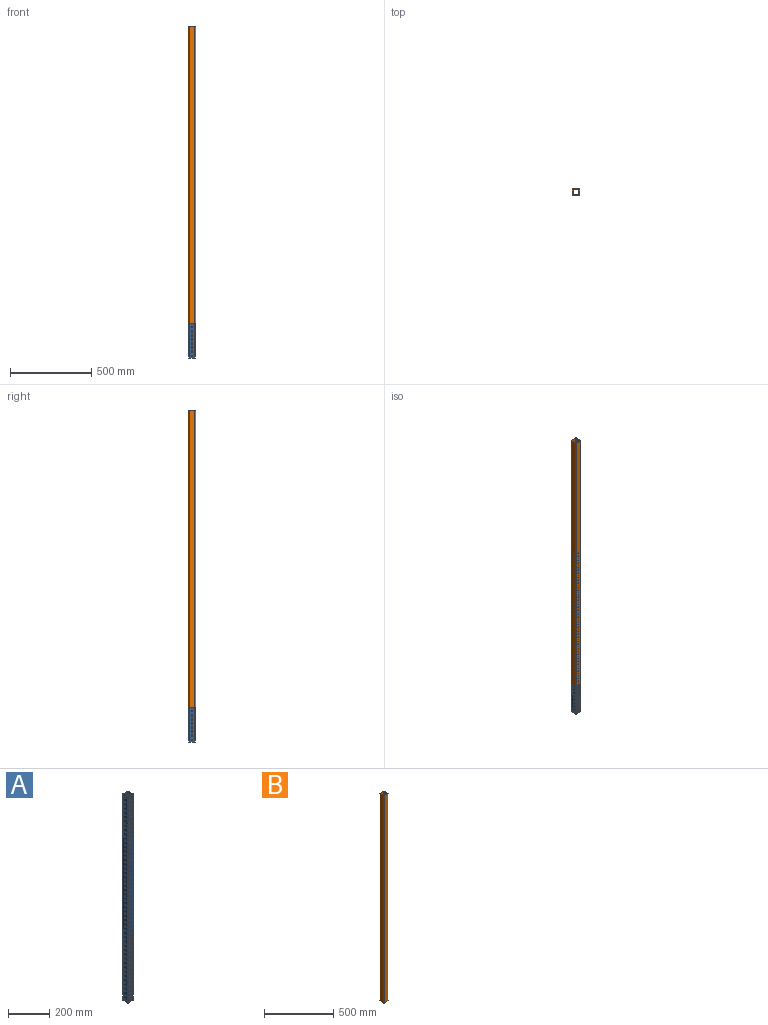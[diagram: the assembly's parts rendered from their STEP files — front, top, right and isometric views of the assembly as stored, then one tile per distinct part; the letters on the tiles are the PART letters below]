
ASSEMBLY  parts=2 mates=1
PART A: 210 faces, bbox 38.1x38.1x1219.2 mm
  f0: cylinder r=5.56mm len=11.11mm, axis (1,0,0), area 93.1mm2, adj f201,f203
  f1: cylinder r=5.56mm len=11.11mm, axis (1,0,0), area 93.1mm2, adj f197,f207
  f2: cylinder r=5.56mm len=11.11mm, axis (1,0,0), area 93.1mm2, adj f201,f203
  f3: cylinder r=5.56mm len=11.11mm, axis (1,0,0), area 93.1mm2, adj f197,f207
  f4: cylinder r=5.56mm len=11.11mm, axis (1,0,0), area 93.1mm2, adj f201,f203
  f5: cylinder r=5.56mm len=11.11mm, axis (1,0,0), area 93.1mm2, adj f197,f207
  f6: cylinder r=5.56mm len=11.11mm, axis (1,0,0), area 93.1mm2, adj f201,f203
  f7: cylinder r=5.56mm len=11.11mm, axis (1,0,0), area 93.1mm2, adj f197,f207
  f8: cylinder r=5.56mm len=11.11mm, axis (1,0,0), area 93.1mm2, adj f201,f203
  f9: cylinder r=5.56mm len=11.11mm, axis (1,0,0), area 93.1mm2, adj f197,f207
  f10: cylinder r=5.56mm len=11.11mm, axis (1,0,0), area 93.1mm2, adj f201,f203
  f11: cylinder r=5.56mm len=11.11mm, axis (1,0,0), area 93.1mm2, adj f197,f207
  f12: cylinder r=5.56mm len=11.11mm, axis (1,0,0), area 93.1mm2, adj f201,f203
  f13: cylinder r=5.56mm len=11.11mm, axis (1,0,0), area 93.1mm2, adj f197,f207
  f14: cylinder r=5.56mm len=11.11mm, axis (1,0,0), area 93.1mm2, adj f201,f203
  f15: cylinder r=5.56mm len=11.11mm, axis (1,0,0), area 93.1mm2, adj f197,f207
  f16: cylinder r=5.56mm len=11.11mm, axis (1,0,0), area 93.1mm2, adj f201,f203
  f17: cylinder r=5.56mm len=11.11mm, axis (1,0,0), area 93.1mm2, adj f197,f207
  f18: cylinder r=5.56mm len=11.11mm, axis (1,0,0), area 93.1mm2, adj f201,f203
  f19: cylinder r=5.56mm len=11.11mm, axis (1,0,0), area 93.1mm2, adj f197,f207
  f20: cylinder r=5.56mm len=11.11mm, axis (1,0,0), area 93.1mm2, adj f201,f203
  f21: cylinder r=5.56mm len=11.11mm, axis (1,0,0), area 93.1mm2, adj f197,f207
  f22: cylinder r=5.56mm len=11.11mm, axis (1,0,0), area 93.1mm2, adj f201,f203
  f23: cylinder r=5.56mm len=11.11mm, axis (1,0,0), area 93.1mm2, adj f197,f207
  f24: cylinder r=5.56mm len=11.11mm, axis (1,0,0), area 93.1mm2, adj f201,f203
  f25: cylinder r=5.56mm len=11.11mm, axis (1,0,0), area 93.1mm2, adj f197,f207
  f26: cylinder r=5.56mm len=11.11mm, axis (1,0,0), area 93.1mm2, adj f201,f203
  f27: cylinder r=5.56mm len=11.11mm, axis (1,0,0), area 93.1mm2, adj f197,f207
  f28: cylinder r=5.56mm len=11.11mm, axis (1,0,0), area 93.1mm2, adj f201,f203
  f29: cylinder r=5.56mm len=11.11mm, axis (1,0,0), area 93.1mm2, adj f197,f207
  f30: cylinder r=5.56mm len=11.11mm, axis (1,0,0), area 93.1mm2, adj f201,f203
  f31: cylinder r=5.56mm len=11.11mm, axis (1,0,0), area 93.1mm2, adj f197,f207
  f32: cylinder r=5.56mm len=11.11mm, axis (1,0,0), area 93.1mm2, adj f201,f203
  f33: cylinder r=5.56mm len=11.11mm, axis (1,0,0), area 93.1mm2, adj f197,f207
  f34: cylinder r=5.56mm len=11.11mm, axis (1,0,0), area 93.1mm2, adj f201,f203
  f35: cylinder r=5.56mm len=11.11mm, axis (1,0,0), area 93.1mm2, adj f197,f207
  f36: cylinder r=5.56mm len=11.11mm, axis (1,0,0), area 93.1mm2, adj f201,f203
  f37: cylinder r=5.56mm len=11.11mm, axis (1,0,0), area 93.1mm2, adj f197,f207
  f38: cylinder r=5.56mm len=11.11mm, axis (1,0,0), area 93.1mm2, adj f201,f203
  f39: cylinder r=5.56mm len=11.11mm, axis (1,0,0), area 93.1mm2, adj f197,f207
  f40: cylinder r=5.56mm len=11.11mm, axis (1,0,0), area 93.1mm2, adj f201,f203
  f41: cylinder r=5.56mm len=11.11mm, axis (1,0,0), area 93.1mm2, adj f197,f207
  f42: cylinder r=5.56mm len=11.11mm, axis (1,0,0), area 93.1mm2, adj f201,f203
  f43: cylinder r=5.56mm len=11.11mm, axis (1,0,0), area 93.1mm2, adj f197,f207
  f44: cylinder r=5.56mm len=11.11mm, axis (1,0,0), area 93.1mm2, adj f201,f203
  f45: cylinder r=5.56mm len=11.11mm, axis (1,0,0), area 93.1mm2, adj f197,f207
  f46: cylinder r=5.56mm len=11.11mm, axis (1,0,0), area 93.1mm2, adj f201,f203
  f47: cylinder r=5.56mm len=11.11mm, axis (1,0,0), area 93.1mm2, adj f197,f207
  f48: cylinder r=5.56mm len=11.11mm, axis (1,0,0), area 93.1mm2, adj f201,f203
  f49: cylinder r=5.56mm len=11.11mm, axis (1,0,0), area 93.1mm2, adj f197,f207
  f50: cylinder r=5.56mm len=11.11mm, axis (1,0,0), area 93.1mm2, adj f201,f203
  f51: cylinder r=5.56mm len=11.11mm, axis (1,0,0), area 93.1mm2, adj f197,f207
  f52: cylinder r=5.56mm len=11.11mm, axis (1,0,0), area 93.1mm2, adj f201,f203
  f53: cylinder r=5.56mm len=11.11mm, axis (1,0,0), area 93.1mm2, adj f197,f207
  f54: cylinder r=5.56mm len=11.11mm, axis (1,0,0), area 93.1mm2, adj f201,f203
  f55: cylinder r=5.56mm len=11.11mm, axis (1,0,0), area 93.1mm2, adj f197,f207
  f56: cylinder r=5.56mm len=11.11mm, axis (1,0,0), area 93.1mm2, adj f201,f203
  f57: cylinder r=5.56mm len=11.11mm, axis (1,0,0), area 93.1mm2, adj f197,f207
  f58: cylinder r=5.56mm len=11.11mm, axis (1,0,0), area 93.1mm2, adj f201,f203
  f59: cylinder r=5.56mm len=11.11mm, axis (1,0,0), area 93.1mm2, adj f197,f207
  f60: cylinder r=5.56mm len=11.11mm, axis (1,0,0), area 93.1mm2, adj f201,f203
  f61: cylinder r=5.56mm len=11.11mm, axis (1,0,0), area 93.1mm2, adj f197,f207
  f62: cylinder r=5.56mm len=11.11mm, axis (1,0,0), area 93.1mm2, adj f201,f203
  f63: cylinder r=5.56mm len=11.11mm, axis (1,0,0), area 93.1mm2, adj f197,f207
  f64: cylinder r=5.56mm len=11.11mm, axis (1,0,0), area 93.1mm2, adj f201,f203
  f65: cylinder r=5.56mm len=11.11mm, axis (1,0,0), area 93.1mm2, adj f197,f207
  f66: cylinder r=5.56mm len=11.11mm, axis (1,0,0), area 93.1mm2, adj f201,f203
  f67: cylinder r=5.56mm len=11.11mm, axis (1,0,0), area 93.1mm2, adj f197,f207
  f68: cylinder r=5.56mm len=11.11mm, axis (1,0,0), area 93.1mm2, adj f201,f203
  f69: cylinder r=5.56mm len=11.11mm, axis (1,0,0), area 93.1mm2, adj f197,f207
  f70: cylinder r=5.56mm len=11.11mm, axis (1,0,0), area 93.1mm2, adj f201,f203
  f71: cylinder r=5.56mm len=11.11mm, axis (1,0,0), area 93.1mm2, adj f197,f207
  f72: cylinder r=5.56mm len=11.11mm, axis (1,0,0), area 93.1mm2, adj f201,f203
  f73: cylinder r=5.56mm len=11.11mm, axis (1,0,0), area 93.1mm2, adj f197,f207
  f74: cylinder r=5.56mm len=11.11mm, axis (1,0,0), area 93.1mm2, adj f201,f203
  f75: cylinder r=5.56mm len=11.11mm, axis (1,0,0), area 93.1mm2, adj f197,f207
  f76: cylinder r=5.56mm len=11.11mm, axis (1,0,0), area 93.1mm2, adj f201,f203
  f77: cylinder r=5.56mm len=11.11mm, axis (1,0,0), area 93.1mm2, adj f197,f207
  f78: cylinder r=5.56mm len=11.11mm, axis (1,0,0), area 93.1mm2, adj f201,f203
  f79: cylinder r=5.56mm len=11.11mm, axis (1,0,0), area 93.1mm2, adj f197,f207
  f80: cylinder r=5.56mm len=11.11mm, axis (1,0,0), area 93.1mm2, adj f201,f203
  f81: cylinder r=5.56mm len=11.11mm, axis (1,0,0), area 93.1mm2, adj f197,f207
  f82: cylinder r=5.56mm len=11.11mm, axis (1,0,0), area 93.1mm2, adj f201,f203
  f83: cylinder r=5.56mm len=11.11mm, axis (1,0,0), area 93.1mm2, adj f197,f207
  f84: cylinder r=5.56mm len=11.11mm, axis (1,0,0), area 93.1mm2, adj f201,f203
  f85: cylinder r=5.56mm len=11.11mm, axis (1,0,0), area 93.1mm2, adj f197,f207
  f86: cylinder r=5.56mm len=11.11mm, axis (1,0,0), area 93.1mm2, adj f201,f203
  f87: cylinder r=5.56mm len=11.11mm, axis (1,0,0), area 93.1mm2, adj f197,f207
  f88: cylinder r=5.56mm len=11.11mm, axis (1,0,0), area 93.1mm2, adj f201,f203
  f89: cylinder r=5.56mm len=11.11mm, axis (1,0,0), area 93.1mm2, adj f197,f207
  f90: cylinder r=5.56mm len=11.11mm, axis (1,0,0), area 93.1mm2, adj f201,f203
  f91: cylinder r=5.56mm len=11.11mm, axis (1,0,0), area 93.1mm2, adj f197,f207
  f92: cylinder r=5.56mm len=11.11mm, axis (1,0,0), area 93.1mm2, adj f201,f203
  f93: cylinder r=5.56mm len=11.11mm, axis (1,0,0), area 93.1mm2, adj f197,f207
  f94: cylinder r=5.56mm len=11.11mm, axis (1,0,0), area 93.1mm2, adj f201,f203
  f95: cylinder r=5.56mm len=11.11mm, axis (1,0,0), area 93.1mm2, adj f197,f207
  f96: cylinder r=5.56mm len=11.11mm, axis (0,1,0), area 93.1mm2, adj f199,f209
  f97: cylinder r=5.56mm len=11.11mm, axis (0,1,0), area 93.1mm2, adj f199,f209
  f98: cylinder r=5.56mm len=11.11mm, axis (0,1,0), area 93.1mm2, adj f199,f209
  f99: cylinder r=5.56mm len=11.11mm, axis (0,1,0), area 93.1mm2, adj f199,f209
  f100: cylinder r=5.56mm len=11.11mm, axis (0,1,0), area 93.1mm2, adj f199,f209
  f101: cylinder r=5.56mm len=11.11mm, axis (0,1,0), area 93.1mm2, adj f199,f209
  f102: cylinder r=5.56mm len=11.11mm, axis (0,1,0), area 93.1mm2, adj f199,f209
  f103: cylinder r=5.56mm len=11.11mm, axis (0,1,0), area 93.1mm2, adj f199,f209
  f104: cylinder r=5.56mm len=11.11mm, axis (0,1,0), area 93.1mm2, adj f199,f209
  f105: cylinder r=5.56mm len=11.11mm, axis (0,1,0), area 93.1mm2, adj f199,f209
  f106: cylinder r=5.56mm len=11.11mm, axis (0,1,0), area 93.1mm2, adj f199,f209
  f107: cylinder r=5.56mm len=11.11mm, axis (0,1,0), area 93.1mm2, adj f199,f209
  f108: cylinder r=5.56mm len=11.11mm, axis (0,1,0), area 93.1mm2, adj f199,f209
  f109: cylinder r=5.56mm len=11.11mm, axis (0,1,0), area 93.1mm2, adj f199,f209
  f110: cylinder r=5.56mm len=11.11mm, axis (0,1,0), area 93.1mm2, adj f199,f209
  f111: cylinder r=5.56mm len=11.11mm, axis (0,1,0), area 93.1mm2, adj f199,f209
  f112: cylinder r=5.56mm len=11.11mm, axis (0,1,0), area 93.1mm2, adj f199,f209
  f113: cylinder r=5.56mm len=11.11mm, axis (0,1,0), area 93.1mm2, adj f199,f209
  f114: cylinder r=5.56mm len=11.11mm, axis (0,1,0), area 93.1mm2, adj f199,f209
  f115: cylinder r=5.56mm len=11.11mm, axis (0,1,0), area 93.1mm2, adj f199,f209
  f116: cylinder r=5.56mm len=11.11mm, axis (0,1,0), area 93.1mm2, adj f199,f209
  f117: cylinder r=5.56mm len=11.11mm, axis (0,1,0), area 93.1mm2, adj f199,f209
  f118: cylinder r=5.56mm len=11.11mm, axis (0,1,0), area 93.1mm2, adj f199,f209
  f119: cylinder r=5.56mm len=11.11mm, axis (0,1,0), area 93.1mm2, adj f199,f209
  f120: cylinder r=5.56mm len=11.11mm, axis (0,1,0), area 93.1mm2, adj f199,f209
  f121: cylinder r=5.56mm len=11.11mm, axis (0,1,0), area 93.1mm2, adj f199,f209
  f122: cylinder r=5.56mm len=11.11mm, axis (0,1,0), area 93.1mm2, adj f199,f209
  f123: cylinder r=5.56mm len=11.11mm, axis (0,1,0), area 93.1mm2, adj f199,f209
  f124: cylinder r=5.56mm len=11.11mm, axis (0,1,0), area 93.1mm2, adj f199,f209
  f125: cylinder r=5.56mm len=11.11mm, axis (0,1,0), area 93.1mm2, adj f199,f209
  f126: cylinder r=5.56mm len=11.11mm, axis (0,1,0), area 93.1mm2, adj f199,f209
  f127: cylinder r=5.56mm len=11.11mm, axis (0,1,0), area 93.1mm2, adj f199,f209
  f128: cylinder r=5.56mm len=11.11mm, axis (0,1,0), area 93.1mm2, adj f199,f209
  f129: cylinder r=5.56mm len=11.11mm, axis (0,1,0), area 93.1mm2, adj f199,f209
  f130: cylinder r=5.56mm len=11.11mm, axis (0,1,0), area 93.1mm2, adj f199,f209
  f131: cylinder r=5.56mm len=11.11mm, axis (0,1,0), area 93.1mm2, adj f199,f209
  f132: cylinder r=5.56mm len=11.11mm, axis (0,1,0), area 93.1mm2, adj f199,f209
  f133: cylinder r=5.56mm len=11.11mm, axis (0,1,0), area 93.1mm2, adj f199,f209
  f134: cylinder r=5.56mm len=11.11mm, axis (0,1,0), area 93.1mm2, adj f199,f209
  f135: cylinder r=5.56mm len=11.11mm, axis (0,1,0), area 93.1mm2, adj f199,f209
  f136: cylinder r=5.56mm len=11.11mm, axis (0,1,0), area 93.1mm2, adj f199,f209
  f137: cylinder r=5.56mm len=11.11mm, axis (0,1,0), area 93.1mm2, adj f199,f209
  f138: cylinder r=5.56mm len=11.11mm, axis (0,1,0), area 93.1mm2, adj f199,f209
  f139: cylinder r=5.56mm len=11.11mm, axis (0,1,0), area 93.1mm2, adj f199,f209
  f140: cylinder r=5.56mm len=11.11mm, axis (0,1,0), area 93.1mm2, adj f199,f209
  f141: cylinder r=5.56mm len=11.11mm, axis (0,1,0), area 93.1mm2, adj f199,f209
  f142: cylinder r=5.56mm len=11.11mm, axis (0,1,0), area 93.1mm2, adj f199,f209
  f143: cylinder r=5.56mm len=11.11mm, axis (0,1,0), area 93.1mm2, adj f195,f205
  f144: cylinder r=5.56mm len=11.11mm, axis (0,1,0), area 93.1mm2, adj f195,f205
  f145: cylinder r=5.56mm len=11.11mm, axis (0,1,0), area 93.1mm2, adj f195,f205
  f146: cylinder r=5.56mm len=11.11mm, axis (0,1,0), area 93.1mm2, adj f195,f205
  f147: cylinder r=5.56mm len=11.11mm, axis (0,1,0), area 93.1mm2, adj f195,f205
  f148: cylinder r=5.56mm len=11.11mm, axis (0,1,0), area 93.1mm2, adj f195,f205
  f149: cylinder r=5.56mm len=11.11mm, axis (0,1,0), area 93.1mm2, adj f195,f205
  f150: cylinder r=5.56mm len=11.11mm, axis (0,1,0), area 93.1mm2, adj f195,f205
  f151: cylinder r=5.56mm len=11.11mm, axis (0,1,0), area 93.1mm2, adj f195,f205
  f152: cylinder r=5.56mm len=11.11mm, axis (0,1,0), area 93.1mm2, adj f195,f205
  f153: cylinder r=5.56mm len=11.11mm, axis (0,1,0), area 93.1mm2, adj f195,f205
  f154: cylinder r=5.56mm len=11.11mm, axis (0,1,0), area 93.1mm2, adj f195,f205
  f155: cylinder r=5.56mm len=11.11mm, axis (0,1,0), area 93.1mm2, adj f195,f205
  f156: cylinder r=5.56mm len=11.11mm, axis (0,1,0), area 93.1mm2, adj f195,f205
  f157: cylinder r=5.56mm len=11.11mm, axis (0,1,0), area 93.1mm2, adj f195,f205
  f158: cylinder r=5.56mm len=11.11mm, axis (0,1,0), area 93.1mm2, adj f195,f205
  f159: cylinder r=5.56mm len=11.11mm, axis (0,1,0), area 93.1mm2, adj f195,f205
  f160: cylinder r=5.56mm len=11.11mm, axis (0,1,0), area 93.1mm2, adj f195,f205
  f161: cylinder r=5.56mm len=11.11mm, axis (0,1,0), area 93.1mm2, adj f195,f205
  f162: cylinder r=5.56mm len=11.11mm, axis (0,1,0), area 93.1mm2, adj f195,f205
  f163: cylinder r=5.56mm len=11.11mm, axis (0,1,0), area 93.1mm2, adj f195,f205
  f164: cylinder r=5.56mm len=11.11mm, axis (0,1,0), area 93.1mm2, adj f195,f205
  f165: cylinder r=5.56mm len=11.11mm, axis (0,1,0), area 93.1mm2, adj f195,f205
  f166: cylinder r=5.56mm len=11.11mm, axis (0,1,0), area 93.1mm2, adj f195,f205
  f167: cylinder r=5.56mm len=11.11mm, axis (0,1,0), area 93.1mm2, adj f195,f205
  f168: cylinder r=5.56mm len=11.11mm, axis (0,1,0), area 93.1mm2, adj f195,f205
  f169: cylinder r=5.56mm len=11.11mm, axis (0,1,0), area 93.1mm2, adj f195,f205
  f170: cylinder r=5.56mm len=11.11mm, axis (0,1,0), area 93.1mm2, adj f195,f205
  f171: cylinder r=5.56mm len=11.11mm, axis (0,1,0), area 93.1mm2, adj f195,f205
  f172: cylinder r=5.56mm len=11.11mm, axis (0,1,0), area 93.1mm2, adj f195,f205
  f173: cylinder r=5.56mm len=11.11mm, axis (0,1,0), area 93.1mm2, adj f195,f205
  f174: cylinder r=5.56mm len=11.11mm, axis (0,1,0), area 93.1mm2, adj f195,f205
  f175: cylinder r=5.56mm len=11.11mm, axis (0,1,0), area 93.1mm2, adj f195,f205
  f176: cylinder r=5.56mm len=11.11mm, axis (0,1,0), area 93.1mm2, adj f195,f205
  f177: cylinder r=5.56mm len=11.11mm, axis (0,1,0), area 93.1mm2, adj f195,f205
  f178: cylinder r=5.56mm len=11.11mm, axis (0,1,0), area 93.1mm2, adj f195,f205
  f179: cylinder r=5.56mm len=11.11mm, axis (0,1,0), area 93.1mm2, adj f195,f205
  f180: cylinder r=5.56mm len=11.11mm, axis (0,1,0), area 93.1mm2, adj f195,f205
  f181: cylinder r=5.56mm len=11.11mm, axis (0,1,0), area 93.1mm2, adj f195,f205
  f182: cylinder r=5.56mm len=11.11mm, axis (0,1,0), area 93.1mm2, adj f195,f205
  f183: cylinder r=5.56mm len=11.11mm, axis (0,1,0), area 93.1mm2, adj f195,f205
  f184: cylinder r=5.56mm len=11.11mm, axis (0,1,0), area 93.1mm2, adj f195,f205
  f185: cylinder r=5.56mm len=11.11mm, axis (0,1,0), area 93.1mm2, adj f195,f205
  f186: cylinder r=5.56mm len=11.11mm, axis (0,1,0), area 93.1mm2, adj f195,f205
  f187: cylinder r=5.56mm len=11.11mm, axis (0,1,0), area 93.1mm2, adj f195,f205
  f188: cylinder r=5.56mm len=11.11mm, axis (0,1,0), area 93.1mm2, adj f195,f205
  f189: cylinder r=5.56mm len=11.11mm, axis (0,1,0), area 93.1mm2, adj f195,f205
  f190: cylinder r=5.56mm len=11.11mm, axis (0,1,0), area 93.1mm2, adj f195,f205
  f191: cylinder r=5.56mm len=11.11mm, axis (0,1,0), area 93.1mm2, adj f199,f209
  f192: plane 38.1x38.1mm, normal (0,0,1), area 364.9mm2, adj f194,f195,f196,f197,f198,f199,f200,f201
  f193: plane 38.1x38.1mm, normal (0,0,-1), area 364.9mm2, adj f194,f195,f196,f197,f198,f199,f200,f201
  f194: cylinder r=4.19mm len=1219.2mm, axis (0,0,-1), area 8026.2mm2, adj f192,f193,f195,f201
  f195: plane 1219.2x29.72mm, normal (0,-1,0), area 31576.8mm2, adj f143,f144,f145,f146,f147,f148,f149,f150
  f196: cylinder r=4.19mm len=1219.2mm, axis (0,0,-1), area 8026.2mm2, adj f192,f193,f195,f197
  f197: plane 1219.2x29.72mm, normal (1,0,0), area 31576.8mm2, adj f1,f3,f5,f7,f9,f11,f13,f15
  f198: cylinder r=4.19mm len=1219.2mm, axis (0,0,-1), area 8026.2mm2, adj f192,f193,f197,f199
  f199: plane 1219.2x29.72mm, normal (0,1,0), area 31576.8mm2, adj f96,f97,f98,f99,f100,f101,f102,f103
  f200: cylinder r=4.19mm len=1219.2mm, axis (0,0,-1), area 8026.2mm2, adj f192,f193,f199,f201
  f201: plane 1219.2x29.72mm, normal (-1,0,0), area 31576.8mm2, adj f0,f2,f4,f6,f8,f10,f12,f14
  f202: cylinder r=1.52mm len=1219.2mm, axis (0,0,-1), area 2918.6mm2, adj f192,f193,f203,f209
  f203: plane 1219.2x29.72mm, normal (1,0,0), area 31576.8mm2, adj f0,f2,f4,f6,f8,f10,f12,f14
  f204: cylinder r=1.52mm len=1219.2mm, axis (0,0,-1), area 2918.6mm2, adj f192,f193,f203,f205
  f205: plane 1219.2x29.72mm, normal (0,1,0), area 31576.8mm2, adj f143,f144,f145,f146,f147,f148,f149,f150
  f206: cylinder r=1.52mm len=1219.2mm, axis (0,0,-1), area 2918.6mm2, adj f192,f193,f205,f207
  f207: plane 1219.2x29.72mm, normal (-1,0,0), area 31576.8mm2, adj f1,f3,f5,f7,f9,f11,f13,f15
  f208: cylinder r=1.52mm len=1219.2mm, axis (0,0,-1), area 2918.6mm2, adj f192,f193,f207,f209
  f209: plane 1219.2x29.72mm, normal (0,-1,0), area 31576.8mm2, adj f96,f97,f98,f99,f100,f101,f102,f103
PART B: 18 faces, bbox 44.5x44.5x1828.8 mm
  f0: plane 44.45x44.45mm, normal (0,0,1), area 432.7mm2, adj f2,f3,f4,f5,f6,f7,f8,f9
  f1: plane 44.45x44.45mm, normal (0,0,-1), area 432.7mm2, adj f2,f3,f4,f5,f6,f7,f8,f9
  f2: cylinder r=4.19mm len=1828.8mm, axis (0,0,-1), area 12039.4mm2, adj f0,f1,f3,f9
  f3: plane 1828.8x36.07mm, normal (0,-1,0), area 65961.2mm2, adj f0,f1,f2,f4
  f4: cylinder r=4.19mm len=1828.8mm, axis (0,0,-1), area 12039.4mm2, adj f0,f1,f3,f5
  f5: plane 1828.8x36.07mm, normal (1,0,0), area 65961.2mm2, adj f0,f1,f4,f6
  f6: cylinder r=4.19mm len=1828.8mm, axis (0,0,-1), area 12039.4mm2, adj f0,f1,f5,f7
  f7: plane 1828.8x36.07mm, normal (0,1,0), area 65961.2mm2, adj f0,f1,f6,f8
  f8: cylinder r=4.19mm len=1828.8mm, axis (0,0,-1), area 12039.4mm2, adj f0,f1,f7,f9
  f9: plane 1828.8x36.07mm, normal (-1,0,0), area 65961.2mm2, adj f0,f1,f2,f8
  f10: cylinder r=1.52mm len=1828.8mm, axis (0,0,-1), area 4378mm2, adj f0,f1,f11,f17
  f11: plane 1828.8x36.07mm, normal (1,0,0), area 65961.2mm2, adj f0,f1,f10,f12
  f12: cylinder r=1.52mm len=1828.8mm, axis (0,0,-1), area 4378mm2, adj f0,f1,f11,f13
  f13: plane 1828.8x36.07mm, normal (0,1,0), area 65961.2mm2, adj f0,f1,f12,f14
  f14: cylinder r=1.52mm len=1828.8mm, axis (0,0,-1), area 4378mm2, adj f0,f1,f13,f15
  f15: plane 1828.8x36.07mm, normal (-1,0,0), area 65961.2mm2, adj f0,f1,f14,f16
  f16: cylinder r=1.52mm len=1828.8mm, axis (0,0,-1), area 4378mm2, adj f0,f1,f15,f17
  f17: plane 1828.8x36.07mm, normal (0,-1,0), area 65961.2mm2, adj f0,f1,f10,f16
PLACE A t=(-758.27,-267.5,-366.51)mm
PLACE B t=(-758.27,-267.5,150.47)mm
MATE slider A.f193 <-> B.f1  axis (0,0,-1) through (-758.27,-267.5,-976.11)mm
